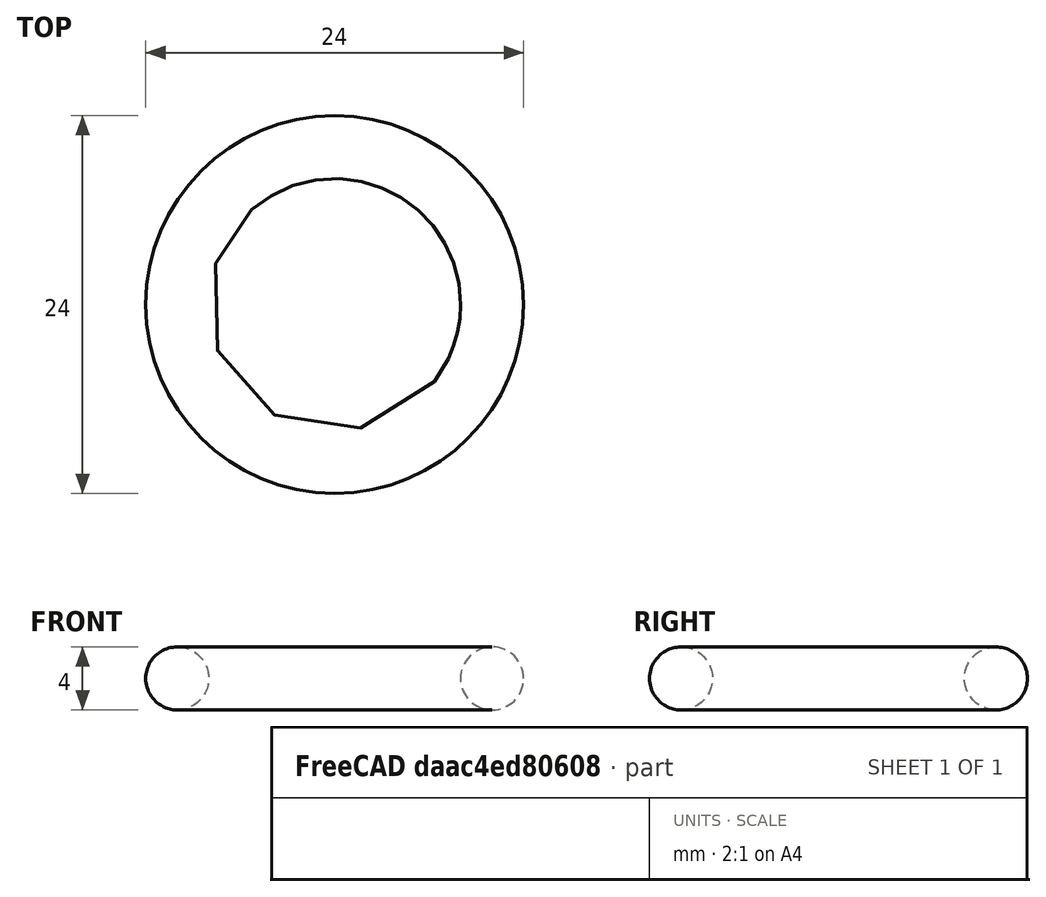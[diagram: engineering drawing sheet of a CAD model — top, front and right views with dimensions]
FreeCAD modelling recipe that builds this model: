
FCSTD DOCUMENT  (FreeCAD 0.19R)
Label: Test_DraftLinkedArray
License: Creative Commons Attribution-ShareAlike
LicenseURL: http://creativecommons.org/licenses/by-sa/4.0/
objects: App::LinkElement×9, Part::Torus×1, Part::FeaturePython×1
note: 1 computed .brp shape members not serialized (recipe doc carries the construction recipe); baked Part::Feature solids carry a one-line shape summary decoded from their .brp

FEATURE [Part::Torus] Torus
  Angle1 = -180
  Angle2 = 180
  Angle3 = 360
  AttacherType = Attacher::AttachEngine3D
  Radius1 = 10
  Radius2 = 2
FEATURE [App::LinkElement] Array_i0
  LinkedObject = -> Torus
FEATURE [App::LinkElement] Array_i1
  LinkPlacement = pos=(0,30,0) rot=(0,0,1;0rad)
  LinkedObject = -> Torus
  Placement = pos=(0,30,0) rot=(0,0,1;0rad)
FEATURE [App::LinkElement] Array_i2
  LinkPlacement = pos=(0,60,0) rot=(0,0,1;0rad)
  LinkedObject = -> Torus
  Placement = pos=(0,60,0) rot=(0,0,1;0rad)
FEATURE [App::LinkElement] Array_i3
  LinkPlacement = pos=(30,0,0) rot=(0,0,1;0rad)
  LinkedObject = -> Torus
  Placement = pos=(30,0,0) rot=(0,0,1;0rad)
FEATURE [App::LinkElement] Array_i4
  LinkPlacement = pos=(30,30,0) rot=(0,0,1;0rad)
  LinkedObject = -> Torus
  Placement = pos=(30,30,0) rot=(0,0,1;0rad)
FEATURE [App::LinkElement] Array_i5
  LinkPlacement = pos=(30,60,0) rot=(0,0,1;0rad)
  LinkedObject = -> Torus
  Placement = pos=(30,60,0) rot=(0,0,1;0rad)
FEATURE [App::LinkElement] Array_i6
  LinkPlacement = pos=(60,0,0) rot=(0,0,1;0rad)
  LinkedObject = -> Torus
  Placement = pos=(60,0,0) rot=(0,0,1;0rad)
FEATURE [App::LinkElement] Array_i7
  LinkPlacement = pos=(60,30,0) rot=(0,0,1;0rad)
  LinkedObject = -> Torus
  Placement = pos=(60,30,0) rot=(0,0,1;0rad)
FEATURE [App::LinkElement] Array_i8
  LinkPlacement = pos=(60,60,0) rot=(0,0,1;0rad)
  LinkedObject = -> Torus
  Placement = pos=(60,60,0) rot=(0,0,1;0rad)
FEATURE [Part::FeaturePython] Array  # Draft array (typed FeaturePython)
  Angle = 360
  ArrayType = 0
  Axis = (0,0,1)
  Base = -> Torus
  Center = (0,0,0)
  Count = 9
  ElementList = -> [Array_i0,Array_i1,Array_i2,Array_i3,Array_i4,Array_i5,Array_i6,Array_i7,Array_i8]
  ExpandArray = true
  Fuse = false
  IntervalAxis = (0,0,0)
  IntervalX = (30,0,0)
  IntervalY = (0,30,0)
  IntervalZ = (0,0,1)
  NumberCircles = 2
  NumberPolar = 1
  NumberX = 3
  NumberY = 3
  NumberZ = 1
  RadialDistance = 1
  Symmetry = 1
  TangentialDistance = 1
